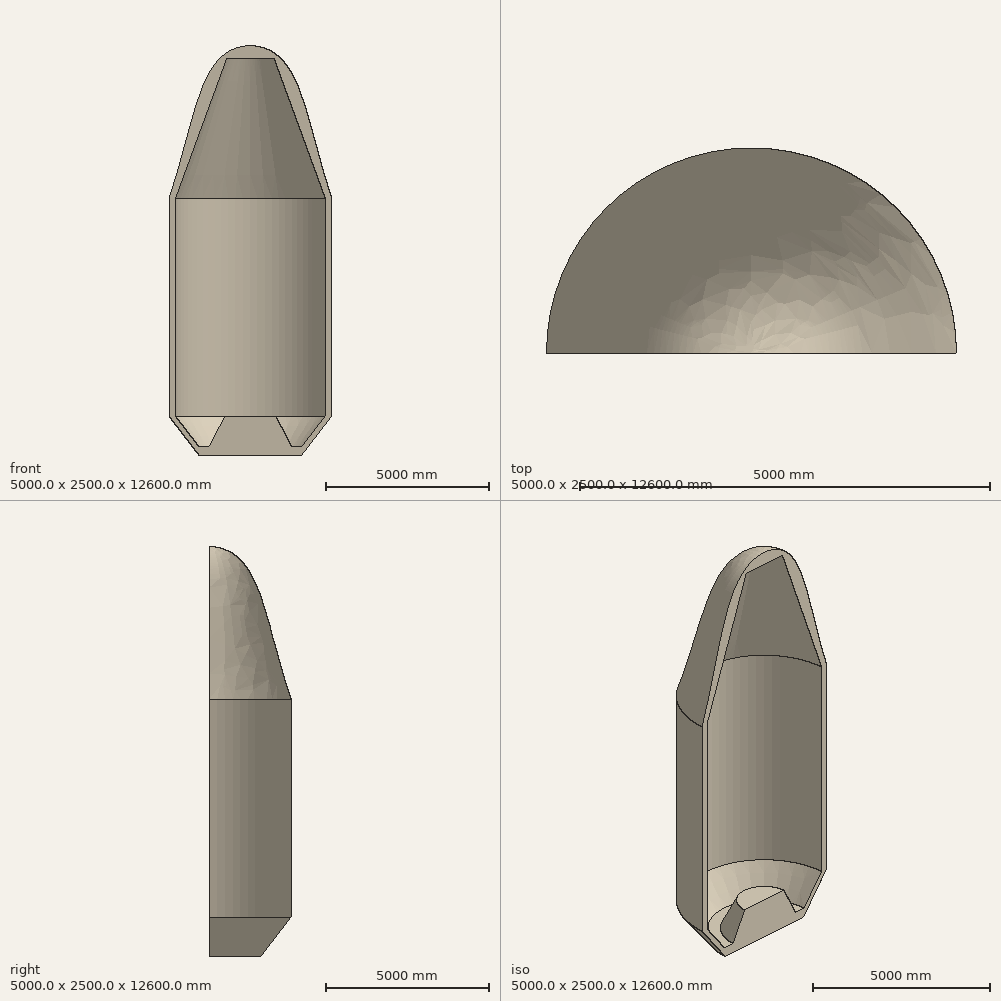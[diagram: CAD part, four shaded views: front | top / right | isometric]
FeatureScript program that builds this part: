
annotation { "Feature Type Name" : "Feature", "Feature Type Description" : "" }
export const myFeature = defineFeature(function(context is Context, id is Id, definition is map)
    precondition{}
    {
        {
            var Q0;
            Q0=qCreatedBy(makeId("Front.planeOp"),FACE);
            var sketch = newSketch(context, id + "F0", { "sketchPlane" : qUnion([Q0])});
            skLineSegment(sketch, "E0", {"start": v(788, 0) * mm, "end": v(1250, -910) * mm});
            skLineSegment(sketch, "E1", {"start": v(1250, -910) * mm, "end": v(1599.84, -910) * mm});
            skLineSegment(sketch, "E2", {"start": v(1599.84, -910) * mm, "end": v(2300, 0) * mm});
            skLineSegment(sketch, "E3", {"start": v(2300, 0) * mm, "end": v(2300, 6700) * mm});
            skLineSegment(sketch, "E4", {"start": v(2300, 6700) * mm, "end": v(725, 11000) * mm});
            skLineSegment(sketch, "E5", {"start": v(725, 11000) * mm, "end": v(0, 11000) * mm});
            skLineSegment(sketch, "E6", {"start": v(0, 11000) * mm, "end": v(0, 11400) * mm});
            skLineSegment(sketch, "E7", {"start": v(788, 0) * mm, "end": v(0, 0) * mm});
            skLineSegment(sketch, "E8", {"start": v(0, 0) * mm, "end": v(0, -1200) * mm});
            skLineSegment(sketch, "E9", {"start": v(0, -1200) * mm, "end": v(1576.71, -1200) * mm});
            skLineSegment(sketch, "E10", {"start": v(1576.71, -1200) * mm, "end": v(2500, 0) * mm});
            skLineSegment(sketch, "E11", {"start": v(2500, 0) * mm, "end": v(2500, 6700) * mm});
            skFitSpline(sketch, "E12", {"points": [v(0, 11400) * mm, v(2500, 6700) * mm], "startDerivative": vector(4871.28, -193.23) * mm, "endDerivative": vector(2457.35, -7188.86) * mm});
            skSolve(sketch);
        }
        {
            var Q0;
            Q0=qCreatedBy(makeId("Front.planeOp"),FACE);
            var sketch = newSketch(context, id + "F1", { "sketchPlane" : qUnion([Q0])});
            skLineSegment(sketch, "E13", {"start": v(0, 0) * mm, "end": v(0, 158.95) * mm});
            skSolve(sketch);
        }
        {
            var Q0;
            Q0=makeQuery(id+"F0.imprint","IMPRINT",FACE,{"disambiguationData":[TD([[makeQuery(id+"F0.imprint","IMPRINT",EDGE,{"derivedFrom":sQuery(id+"F0.wireOp",EDGE,"E0")}),-1.0]])]});
            var Q1;
            Q1=sQuery(id+"F1.wireOp",EDGE,"E13");
            revolve(context, id + "F2", {"entities" : qUnion([Q0]), "axis" : qUnion([Q1]), "revolveType" : RevolveType.ONE_DIRECTION, "angle" : 180 * degree});
        }
    });
